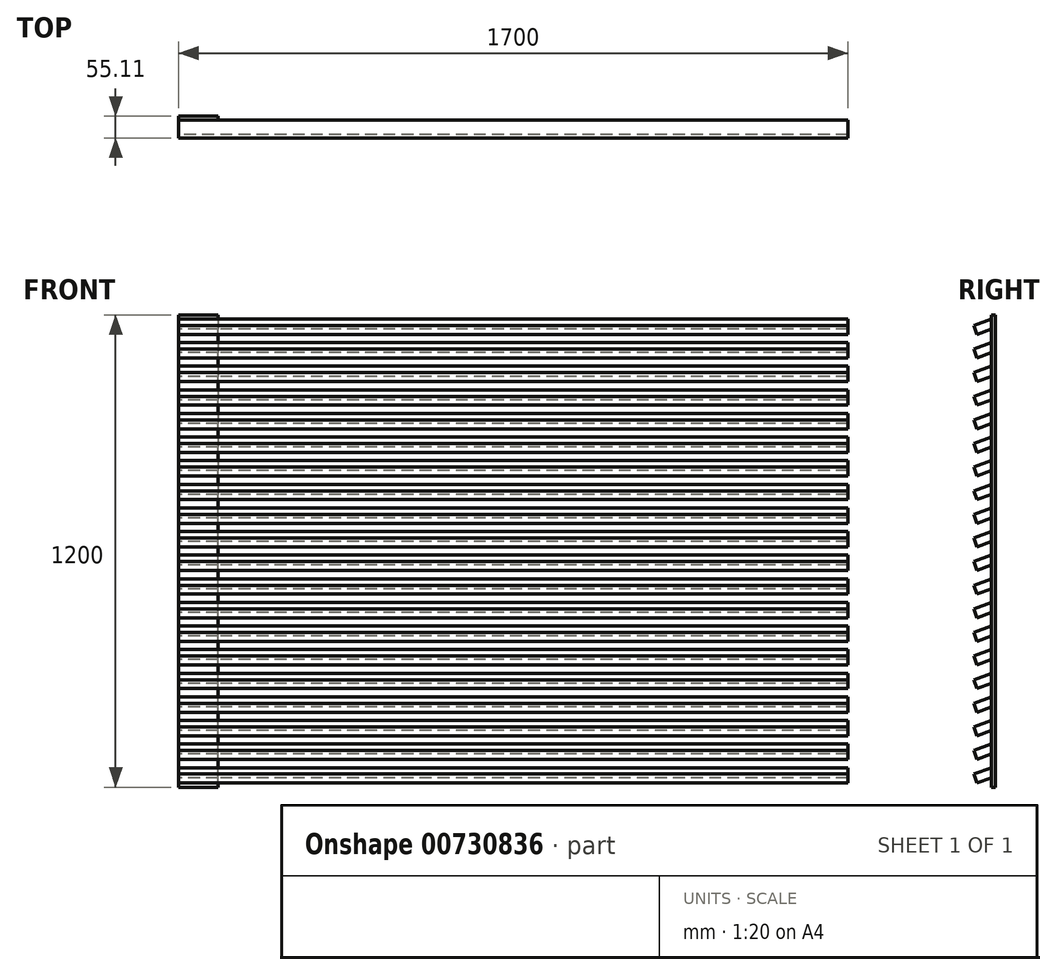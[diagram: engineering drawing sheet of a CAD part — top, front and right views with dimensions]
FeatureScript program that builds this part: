
annotation { "Feature Type Name" : "Feature", "Feature Type Description" : "" }
export const myFeature = defineFeature(function(context is Context, id is Id, definition is map)
    precondition{}
    {
        {
            var Q0;
            Q0=qCreatedBy(makeId("Right.planeOp"),FACE);
            var sketch = newSketch(context, id + "F0", { "sketchPlane" : qUnion([Q0])});
            skLineSegment(sketch, "E0.bottom", {"start": v(0, 0) * mm, "end": v(10, 0) * mm});
            skLineSegment(sketch, "E0.top", {"start": v(0, 1200) * mm, "end": v(10, 1200) * mm});
            skLineSegment(sketch, "E0.left", {"start": v(0, 0) * mm, "end": v(0, 1200) * mm});
            skLineSegment(sketch, "E0.right", {"start": v(10, 0) * mm, "end": v(10, 1200) * mm});
            skSolve(sketch);
        }
        {
            var Q0;
            Q0 = qSketchRegion(id + "F0", true);
            extrude(context, id + "F1", {"entities" : qUnion([Q0]), "depth" : 100 * mm, "offsetDistance" : 25 * mm});
        }
        {
            var Q0;
            Q0=qCreatedBy(makeId("Right.planeOp"),FACE);
            var sketch = newSketch(context, id + "F2", { "sketchPlane" : qUnion([Q0])});
            skLineSegment(sketch, "E1", {"start": v(0, 49.9) * mm, "end": v(-45.1, 33.48) * mm});
            skLineSegment(sketch, "E2", {"start": v(-45.1, 33.48) * mm, "end": v(-36.9, 10.92) * mm});
            skLineSegment(sketch, "E3", {"start": v(-36.9, 10.92) * mm, "end": v(0, 24.35) * mm});
            skLineSegment(sketch, "E4", {"start": v(0, 24.35) * mm, "end": v(0, 24.35) * mm});
            skLineSegment(sketch, "E5", {"start": v(0, 24.35) * mm, "end": v(0, 49.9) * mm});
            skLineSegment(sketch, "E6.0.1.0", {"start": v(-36.9, 70.92) * mm, "end": v(0, 84.35) * mm});
            skLineSegment(sketch, "E6.0.1.1", {"start": v(-45.1, 93.48) * mm, "end": v(-36.9, 70.92) * mm});
            skLineSegment(sketch, "E6.0.1.2", {"start": v(0, 84.35) * mm, "end": v(0, 109.9) * mm});
            skLineSegment(sketch, "E6.0.1.3", {"start": v(0, 109.9) * mm, "end": v(-45.1, 93.48) * mm});
            skLineSegment(sketch, "E6.0.2.0", {"start": v(-36.9, 130.92) * mm, "end": v(0, 144.35) * mm});
            skLineSegment(sketch, "E6.0.2.1", {"start": v(-45.1, 153.48) * mm, "end": v(-36.9, 130.92) * mm});
            skLineSegment(sketch, "E6.0.2.2", {"start": v(0, 144.35) * mm, "end": v(0, 169.9) * mm});
            skLineSegment(sketch, "E6.0.2.3", {"start": v(0, 169.9) * mm, "end": v(-45.1, 153.48) * mm});
            skLineSegment(sketch, "E6.0.3.0", {"start": v(-36.9, 190.92) * mm, "end": v(0, 204.35) * mm});
            skLineSegment(sketch, "E6.0.3.1", {"start": v(-45.1, 213.48) * mm, "end": v(-36.9, 190.92) * mm});
            skLineSegment(sketch, "E6.0.3.2", {"start": v(0, 204.35) * mm, "end": v(0, 229.9) * mm});
            skLineSegment(sketch, "E6.0.3.3", {"start": v(0, 229.9) * mm, "end": v(-45.1, 213.48) * mm});
            skLineSegment(sketch, "E6.0.4.0", {"start": v(-36.9, 250.92) * mm, "end": v(0, 264.35) * mm});
            skLineSegment(sketch, "E6.0.4.1", {"start": v(-45.1, 273.48) * mm, "end": v(-36.9, 250.92) * mm});
            skLineSegment(sketch, "E6.0.4.2", {"start": v(0, 264.35) * mm, "end": v(0, 289.9) * mm});
            skLineSegment(sketch, "E6.0.4.3", {"start": v(0, 289.9) * mm, "end": v(-45.1, 273.48) * mm});
            skLineSegment(sketch, "E6.0.5.0", {"start": v(-36.9, 310.92) * mm, "end": v(0, 324.35) * mm});
            skLineSegment(sketch, "E6.0.5.1", {"start": v(-45.1, 333.48) * mm, "end": v(-36.9, 310.92) * mm});
            skLineSegment(sketch, "E6.0.5.2", {"start": v(0, 324.35) * mm, "end": v(0, 349.9) * mm});
            skLineSegment(sketch, "E6.0.5.3", {"start": v(0, 349.9) * mm, "end": v(-45.1, 333.48) * mm});
            skLineSegment(sketch, "E6.0.6.0", {"start": v(-36.9, 370.92) * mm, "end": v(0, 384.35) * mm});
            skLineSegment(sketch, "E6.0.6.1", {"start": v(-45.1, 393.48) * mm, "end": v(-36.9, 370.92) * mm});
            skLineSegment(sketch, "E6.0.6.2", {"start": v(0, 384.35) * mm, "end": v(0, 409.9) * mm});
            skLineSegment(sketch, "E6.0.6.3", {"start": v(0, 409.9) * mm, "end": v(-45.1, 393.48) * mm});
            skLineSegment(sketch, "E6.0.7.0", {"start": v(-36.9, 430.92) * mm, "end": v(0, 444.35) * mm});
            skLineSegment(sketch, "E6.0.7.1", {"start": v(-45.1, 453.48) * mm, "end": v(-36.9, 430.92) * mm});
            skLineSegment(sketch, "E6.0.7.2", {"start": v(0, 444.35) * mm, "end": v(0, 469.9) * mm});
            skLineSegment(sketch, "E6.0.7.3", {"start": v(0, 469.9) * mm, "end": v(-45.1, 453.48) * mm});
            skLineSegment(sketch, "E6.0.8.0", {"start": v(-36.9, 490.92) * mm, "end": v(0, 504.35) * mm});
            skLineSegment(sketch, "E6.0.8.1", {"start": v(-45.1, 513.48) * mm, "end": v(-36.9, 490.92) * mm});
            skLineSegment(sketch, "E6.0.8.2", {"start": v(0, 504.35) * mm, "end": v(0, 529.9) * mm});
            skLineSegment(sketch, "E6.0.8.3", {"start": v(0, 529.9) * mm, "end": v(-45.1, 513.48) * mm});
            skLineSegment(sketch, "E6.0.9.0", {"start": v(-36.9, 550.92) * mm, "end": v(0, 564.35) * mm});
            skLineSegment(sketch, "E6.0.9.1", {"start": v(-45.1, 573.48) * mm, "end": v(-36.9, 550.92) * mm});
            skLineSegment(sketch, "E6.0.9.2", {"start": v(0, 564.35) * mm, "end": v(0, 589.9) * mm});
            skLineSegment(sketch, "E6.0.9.3", {"start": v(0, 589.9) * mm, "end": v(-45.1, 573.48) * mm});
            skLineSegment(sketch, "E6.0.10.0", {"start": v(-36.9, 610.92) * mm, "end": v(0, 624.35) * mm});
            skLineSegment(sketch, "E6.0.10.1", {"start": v(-45.1, 633.48) * mm, "end": v(-36.9, 610.92) * mm});
            skLineSegment(sketch, "E6.0.10.2", {"start": v(0, 624.35) * mm, "end": v(0, 649.9) * mm});
            skLineSegment(sketch, "E6.0.10.3", {"start": v(0, 649.9) * mm, "end": v(-45.1, 633.48) * mm});
            skLineSegment(sketch, "E6.0.11.0", {"start": v(-36.9, 670.92) * mm, "end": v(0, 684.35) * mm});
            skLineSegment(sketch, "E6.0.11.1", {"start": v(-45.1, 693.48) * mm, "end": v(-36.9, 670.92) * mm});
            skLineSegment(sketch, "E6.0.11.2", {"start": v(0, 684.35) * mm, "end": v(0, 709.9) * mm});
            skLineSegment(sketch, "E6.0.11.3", {"start": v(0, 709.9) * mm, "end": v(-45.1, 693.48) * mm});
            skLineSegment(sketch, "E6.0.12.0", {"start": v(-36.9, 730.92) * mm, "end": v(0, 744.35) * mm});
            skLineSegment(sketch, "E6.0.12.1", {"start": v(-45.1, 753.48) * mm, "end": v(-36.9, 730.92) * mm});
            skLineSegment(sketch, "E6.0.12.2", {"start": v(0, 744.35) * mm, "end": v(0, 769.9) * mm});
            skLineSegment(sketch, "E6.0.12.3", {"start": v(0, 769.9) * mm, "end": v(-45.1, 753.48) * mm});
            skLineSegment(sketch, "E6.0.13.0", {"start": v(-36.9, 790.92) * mm, "end": v(0, 804.35) * mm});
            skLineSegment(sketch, "E6.0.13.1", {"start": v(-45.1, 813.48) * mm, "end": v(-36.9, 790.92) * mm});
            skLineSegment(sketch, "E6.0.13.2", {"start": v(0, 804.35) * mm, "end": v(0, 829.9) * mm});
            skLineSegment(sketch, "E6.0.13.3", {"start": v(0, 829.9) * mm, "end": v(-45.1, 813.48) * mm});
            skLineSegment(sketch, "E6.0.14.0", {"start": v(-36.9, 850.92) * mm, "end": v(0, 864.35) * mm});
            skLineSegment(sketch, "E6.0.14.1", {"start": v(-45.1, 873.48) * mm, "end": v(-36.9, 850.92) * mm});
            skLineSegment(sketch, "E6.0.14.2", {"start": v(0, 864.35) * mm, "end": v(0, 889.9) * mm});
            skLineSegment(sketch, "E6.0.14.3", {"start": v(0, 889.9) * mm, "end": v(-45.1, 873.48) * mm});
            skLineSegment(sketch, "E6.0.15.0", {"start": v(-36.9, 910.92) * mm, "end": v(0, 924.35) * mm});
            skLineSegment(sketch, "E6.0.15.1", {"start": v(-45.1, 933.48) * mm, "end": v(-36.9, 910.92) * mm});
            skLineSegment(sketch, "E6.0.15.2", {"start": v(0, 924.35) * mm, "end": v(0, 949.9) * mm});
            skLineSegment(sketch, "E6.0.15.3", {"start": v(0, 949.9) * mm, "end": v(-45.1, 933.48) * mm});
            skLineSegment(sketch, "E6.0.16.0", {"start": v(-36.9, 970.92) * mm, "end": v(0, 984.35) * mm});
            skLineSegment(sketch, "E6.0.16.1", {"start": v(-45.1, 993.48) * mm, "end": v(-36.9, 970.92) * mm});
            skLineSegment(sketch, "E6.0.16.2", {"start": v(0, 984.35) * mm, "end": v(0, 1009.9) * mm});
            skLineSegment(sketch, "E6.0.16.3", {"start": v(0, 1009.9) * mm, "end": v(-45.1, 993.48) * mm});
            skLineSegment(sketch, "E6.0.17.0", {"start": v(-36.9, 1030.92) * mm, "end": v(0, 1044.35) * mm});
            skLineSegment(sketch, "E6.0.17.1", {"start": v(-45.1, 1053.48) * mm, "end": v(-36.9, 1030.92) * mm});
            skLineSegment(sketch, "E6.0.17.2", {"start": v(0, 1044.35) * mm, "end": v(0, 1069.9) * mm});
            skLineSegment(sketch, "E6.0.17.3", {"start": v(0, 1069.9) * mm, "end": v(-45.1, 1053.48) * mm});
            skLineSegment(sketch, "E6.0.18.0", {"start": v(-36.9, 1090.92) * mm, "end": v(0, 1104.35) * mm});
            skLineSegment(sketch, "E6.0.18.1", {"start": v(-45.1, 1113.48) * mm, "end": v(-36.9, 1090.92) * mm});
            skLineSegment(sketch, "E6.0.18.2", {"start": v(0, 1104.35) * mm, "end": v(0, 1129.9) * mm});
            skLineSegment(sketch, "E6.0.18.3", {"start": v(0, 1129.9) * mm, "end": v(-45.1, 1113.48) * mm});
            skLineSegment(sketch, "E6.0.19.0", {"start": v(-36.9, 1150.92) * mm, "end": v(0, 1164.35) * mm});
            skLineSegment(sketch, "E6.0.19.1", {"start": v(-45.1, 1173.48) * mm, "end": v(-36.9, 1150.92) * mm});
            skLineSegment(sketch, "E6.0.19.2", {"start": v(0, 1164.35) * mm, "end": v(0, 1189.9) * mm});
            skLineSegment(sketch, "E6.0.19.3", {"start": v(0, 1189.9) * mm, "end": v(-45.1, 1173.48) * mm});
            skLineSegment(sketch, "E6.direction1", {"start": v(-45.1, 33.48) * mm, "end": v(-20.1, 33.48) * mm, "construction": true});
            skLineSegment(sketch, "E6.direction2", {"start": v(-45.1, 33.48) * mm, "end": v(-45.1, 93.48) * mm, "construction": true});
            skSolve(sketch);
        }
        {
            var Q0;
            Q0=makeQuery(id+"F2.imprint","IMPRINT",FACE,{"disambiguationData":[TD([[makeQuery(id+"F2.imprint","IMPRINT",EDGE,{"derivedFrom":sQuery(id+"F2.wireOp",EDGE,"E1")}),1.0]])]});
            var Q1;
            Q1=makeQuery(id+"F2.imprint","IMPRINT",FACE,{"disambiguationData":[TD([[makeQuery(id+"F2.imprint","IMPRINT",EDGE,{"derivedFrom":sQuery(id+"F2.wireOp",EDGE,"E6.0.1.0")}),1.0]])]});
            var Q2;
            Q2=makeQuery(id+"F2.imprint","IMPRINT",FACE,{"disambiguationData":[TD([[makeQuery(id+"F2.imprint","IMPRINT",EDGE,{"derivedFrom":sQuery(id+"F2.wireOp",EDGE,"E6.0.2.0")}),1.0]])]});
            var Q3;
            Q3=makeQuery(id+"F2.imprint","IMPRINT",FACE,{"disambiguationData":[TD([[makeQuery(id+"F2.imprint","IMPRINT",EDGE,{"derivedFrom":sQuery(id+"F2.wireOp",EDGE,"E6.0.3.0")}),1.0]])]});
            var Q4;
            Q4=makeQuery(id+"F2.imprint","IMPRINT",FACE,{"disambiguationData":[TD([[makeQuery(id+"F2.imprint","IMPRINT",EDGE,{"derivedFrom":sQuery(id+"F2.wireOp",EDGE,"E6.0.4.0")}),1.0]])]});
            var Q5;
            Q5=makeQuery(id+"F2.imprint","IMPRINT",FACE,{"disambiguationData":[TD([[makeQuery(id+"F2.imprint","IMPRINT",EDGE,{"derivedFrom":sQuery(id+"F2.wireOp",EDGE,"E6.0.6.0")}),1.0]])]});
            var Q6;
            Q6=makeQuery(id+"F2.imprint","IMPRINT",FACE,{"disambiguationData":[TD([[makeQuery(id+"F2.imprint","IMPRINT",EDGE,{"derivedFrom":sQuery(id+"F2.wireOp",EDGE,"E6.0.7.0")}),1.0]])]});
            var Q7;
            Q7=makeQuery(id+"F2.imprint","IMPRINT",FACE,{"disambiguationData":[TD([[makeQuery(id+"F2.imprint","IMPRINT",EDGE,{"derivedFrom":sQuery(id+"F2.wireOp",EDGE,"E6.0.5.0")}),1.0]])]});
            var Q8;
            Q8=makeQuery(id+"F2.imprint","IMPRINT",FACE,{"disambiguationData":[TD([[makeQuery(id+"F2.imprint","IMPRINT",EDGE,{"derivedFrom":sQuery(id+"F2.wireOp",EDGE,"E6.0.8.0")}),1.0]])]});
            var Q9;
            Q9=makeQuery(id+"F2.imprint","IMPRINT",FACE,{"disambiguationData":[TD([[makeQuery(id+"F2.imprint","IMPRINT",EDGE,{"derivedFrom":sQuery(id+"F2.wireOp",EDGE,"E6.0.10.0")}),1.0]])]});
            var Q10;
            Q10=makeQuery(id+"F2.imprint","IMPRINT",FACE,{"disambiguationData":[TD([[makeQuery(id+"F2.imprint","IMPRINT",EDGE,{"derivedFrom":sQuery(id+"F2.wireOp",EDGE,"E6.0.9.0")}),1.0]])]});
            var Q11;
            Q11=makeQuery(id+"F2.imprint","IMPRINT",FACE,{"disambiguationData":[TD([[makeQuery(id+"F2.imprint","IMPRINT",EDGE,{"derivedFrom":sQuery(id+"F2.wireOp",EDGE,"E6.0.11.0")}),1.0]])]});
            var Q12;
            Q12=makeQuery(id+"F2.imprint","IMPRINT",FACE,{"disambiguationData":[TD([[makeQuery(id+"F2.imprint","IMPRINT",EDGE,{"derivedFrom":sQuery(id+"F2.wireOp",EDGE,"E6.0.12.0")}),1.0]])]});
            var Q13;
            Q13=makeQuery(id+"F2.imprint","IMPRINT",FACE,{"disambiguationData":[TD([[makeQuery(id+"F2.imprint","IMPRINT",EDGE,{"derivedFrom":sQuery(id+"F2.wireOp",EDGE,"E6.0.15.0")}),1.0]])]});
            var Q14;
            Q14=makeQuery(id+"F2.imprint","IMPRINT",FACE,{"disambiguationData":[TD([[makeQuery(id+"F2.imprint","IMPRINT",EDGE,{"derivedFrom":sQuery(id+"F2.wireOp",EDGE,"E6.0.13.0")}),1.0]])]});
            var Q15;
            Q15=makeQuery(id+"F2.imprint","IMPRINT",FACE,{"disambiguationData":[TD([[makeQuery(id+"F2.imprint","IMPRINT",EDGE,{"derivedFrom":sQuery(id+"F2.wireOp",EDGE,"E6.0.14.0")}),1.0]])]});
            var Q16;
            Q16=makeQuery(id+"F2.imprint","IMPRINT",FACE,{"disambiguationData":[TD([[makeQuery(id+"F2.imprint","IMPRINT",EDGE,{"derivedFrom":sQuery(id+"F2.wireOp",EDGE,"E6.0.19.0")}),1.0]])]});
            var Q17;
            Q17=makeQuery(id+"F2.imprint","IMPRINT",FACE,{"disambiguationData":[TD([[makeQuery(id+"F2.imprint","IMPRINT",EDGE,{"derivedFrom":sQuery(id+"F2.wireOp",EDGE,"E6.0.18.0")}),1.0]])]});
            var Q18;
            Q18=makeQuery(id+"F2.imprint","IMPRINT",FACE,{"disambiguationData":[TD([[makeQuery(id+"F2.imprint","IMPRINT",EDGE,{"derivedFrom":sQuery(id+"F2.wireOp",EDGE,"E6.0.17.0")}),1.0]])]});
            var Q19;
            Q19=makeQuery(id+"F2.imprint","IMPRINT",FACE,{"disambiguationData":[TD([[makeQuery(id+"F2.imprint","IMPRINT",EDGE,{"derivedFrom":sQuery(id+"F2.wireOp",EDGE,"E6.0.16.0")}),1.0]])]});
            extrude(context, id + "F3", {"entities" : qUnion([Q0, Q1, Q2, Q3, Q4, Q5, Q6, Q7, Q8, Q9, Q10, Q11, Q12, Q13, Q14, Q15, Q16, Q17, Q18, Q19]), "operationType" : NewBodyOperationType.ADD, "depth" : 1700 * mm, "offsetDistance" : 25 * mm});
        }
    });
